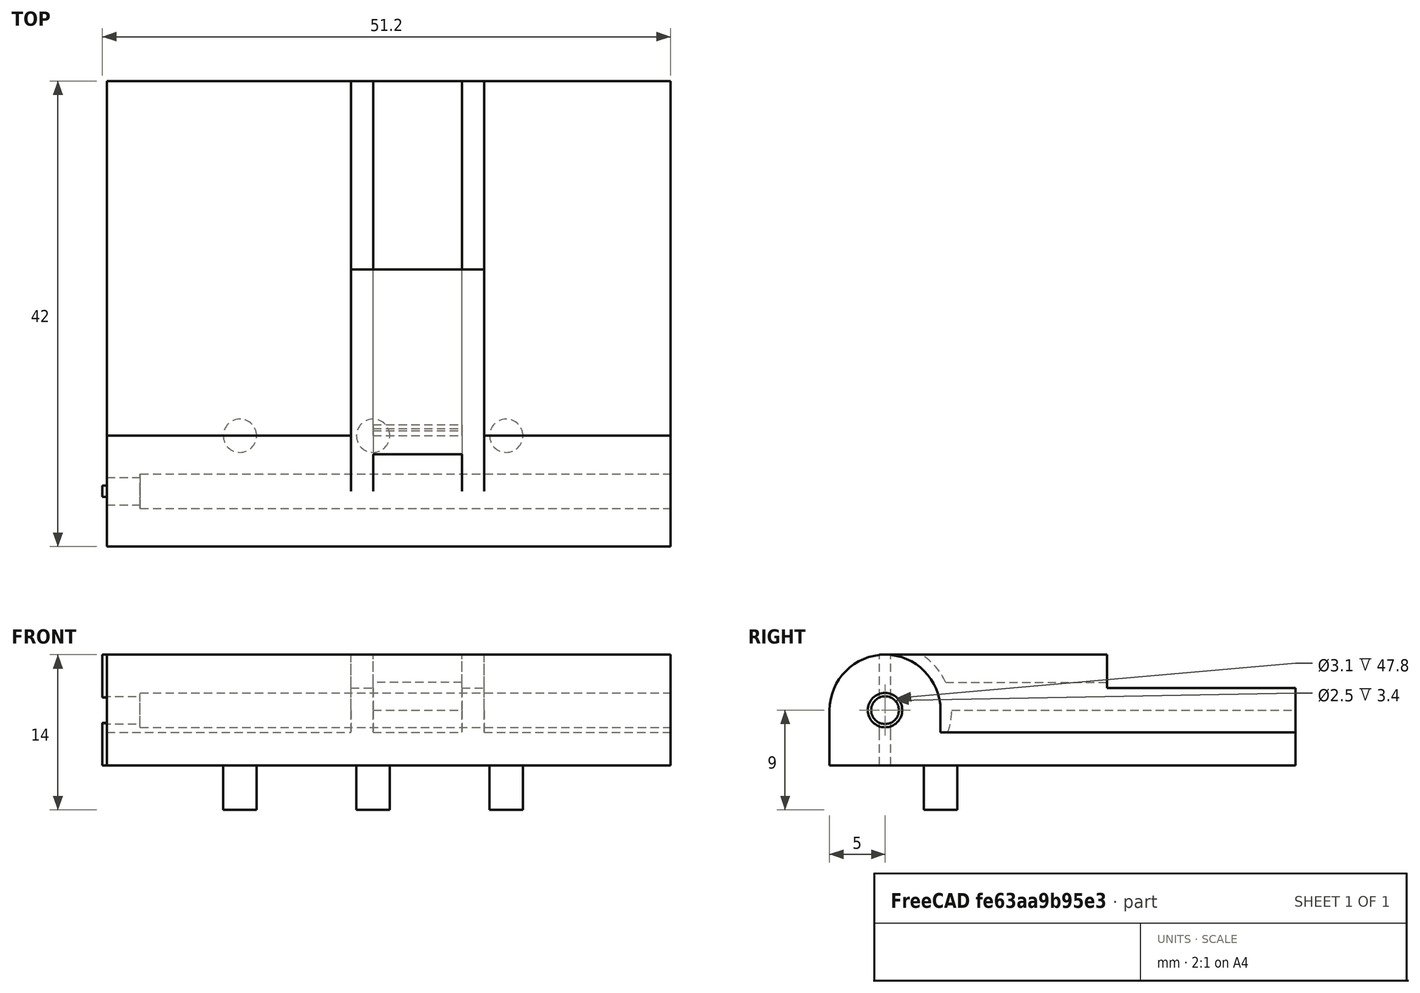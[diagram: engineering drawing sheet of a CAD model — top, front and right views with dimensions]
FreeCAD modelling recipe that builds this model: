
FCSTD DOCUMENT  (FreeCAD 0.16R6707 (Git))
Label: xmaxx-bumber-right
License: All rights reserved
LicenseURL: http://en.wikipedia.org/wiki/All_rights_reserved
objects: Part::Cylinder×7, Part::Box×6, Part::Cut×5, Part::MultiFuse×4
note: 22 computed .brp shape members not serialized (recipe doc carries the construction recipe); baked Part::Feature solids carry a one-line shape summary decoded from their .brp

FEATURE [Part::Box] Box  label="Cube"
  Height = 3
  Length = 50.8
  Width = 42
FEATURE [Part::Box] Box001  label="Cube001"
  Height = 2
  Length = 50.8
  Placement = pos=(0,0,3) rot=(0,0,1;0rad)
  Width = 10
FEATURE [Part::Cylinder] Cylinder
  Angle = 360
  Height = 50.8
  Placement = pos=(0,5,5) rot=(0,1,0;1.5708rad)
  Radius = 5
FEATURE [Part::Cylinder] Cylinder001
  Angle = 360
  Height = 50.8
  Placement = pos=(3,5,5) rot=(0,1,0;1.5708rad)
  Radius = 1.55
FEATURE [Part::Cylinder] Cylinder002
  Angle = 360
  Height = 10
  Placement = pos=(-1,5,5) rot=(0,1,0;1.5708rad)
  Radius = 1.25
FEATURE [Part::Box] Box002  label="Cube002"
  Height = 10
  Length = 0.4
  Placement = pos=(-0.4,4.5,0) rot=(0,0,1;0rad)
  Width = 1
FEATURE [Part::Box] Box003  label="Cube003"
  Height = 10
  Length = 12
  Placement = pos=(22,5,0) rot=(0,0,1;0rad)
  Width = 37
FEATURE [Part::Box] Box004  label="Cube004"
  Height = 2.5
  Length = 8
  Placement = pos=(24,10,5) rot=(0,0,1;0rad)
  Width = 50
FEATURE [Part::Box] Box005  label="Cube005"
  Height = 3
  Length = 12
  Placement = pos=(22,25,7) rot=(0,0,1;0rad)
  Width = 18
FEATURE [Part::Cut] Cut
  Base = -> Box003
  Tool = -> Box004
FEATURE [Part::Cut] Cut001
  Base = -> Cut
  Tool = -> Box005
FEATURE [Part::Cylinder] Cylinder003
  Angle = 360
  Height = 8
  Placement = pos=(24,5,5) rot=(0,1,0;1.5708rad)
  Radius = 6
FEATURE [Part::Cut] Cut002
  Base = -> Cut001
  Tool = -> Cylinder003
FEATURE [Part::MultiFuse] Fusion
  Shapes = -> [Box,Box001,Cylinder]
FEATURE [Part::MultiFuse] Fusion001
  Shapes = -> [Fusion,Box002]
FEATURE [Part::MultiFuse] Fusion002
  Shapes = -> [Fusion001,Cut002]
FEATURE [Part::Cut] Cut003
  Base = -> Fusion002
  Tool = -> Cylinder001
FEATURE [Part::Cut] Cut004
  Base = -> Cut003
  Tool = -> Cylinder002
FEATURE [Part::Cylinder] Cylinder004
  Angle = 360
  Height = 4
  Placement = pos=(12,10,-4) rot=(0,0,1;0rad)
  Radius = 1.5
FEATURE [Part::Cylinder] Cylinder005
  Angle = 360
  Height = 4
  Placement = pos=(24,10,-4) rot=(0,0,1;0rad)
  Radius = 1.5
FEATURE [Part::Cylinder] Cylinder006
  Angle = 360
  Height = 4
  Placement = pos=(36,10,-4) rot=(0,0,1;0rad)
  Radius = 1.5
FEATURE [Part::MultiFuse] Fusion003
  Shapes = -> [Cut004,Cylinder004,Cylinder005,Cylinder006]
